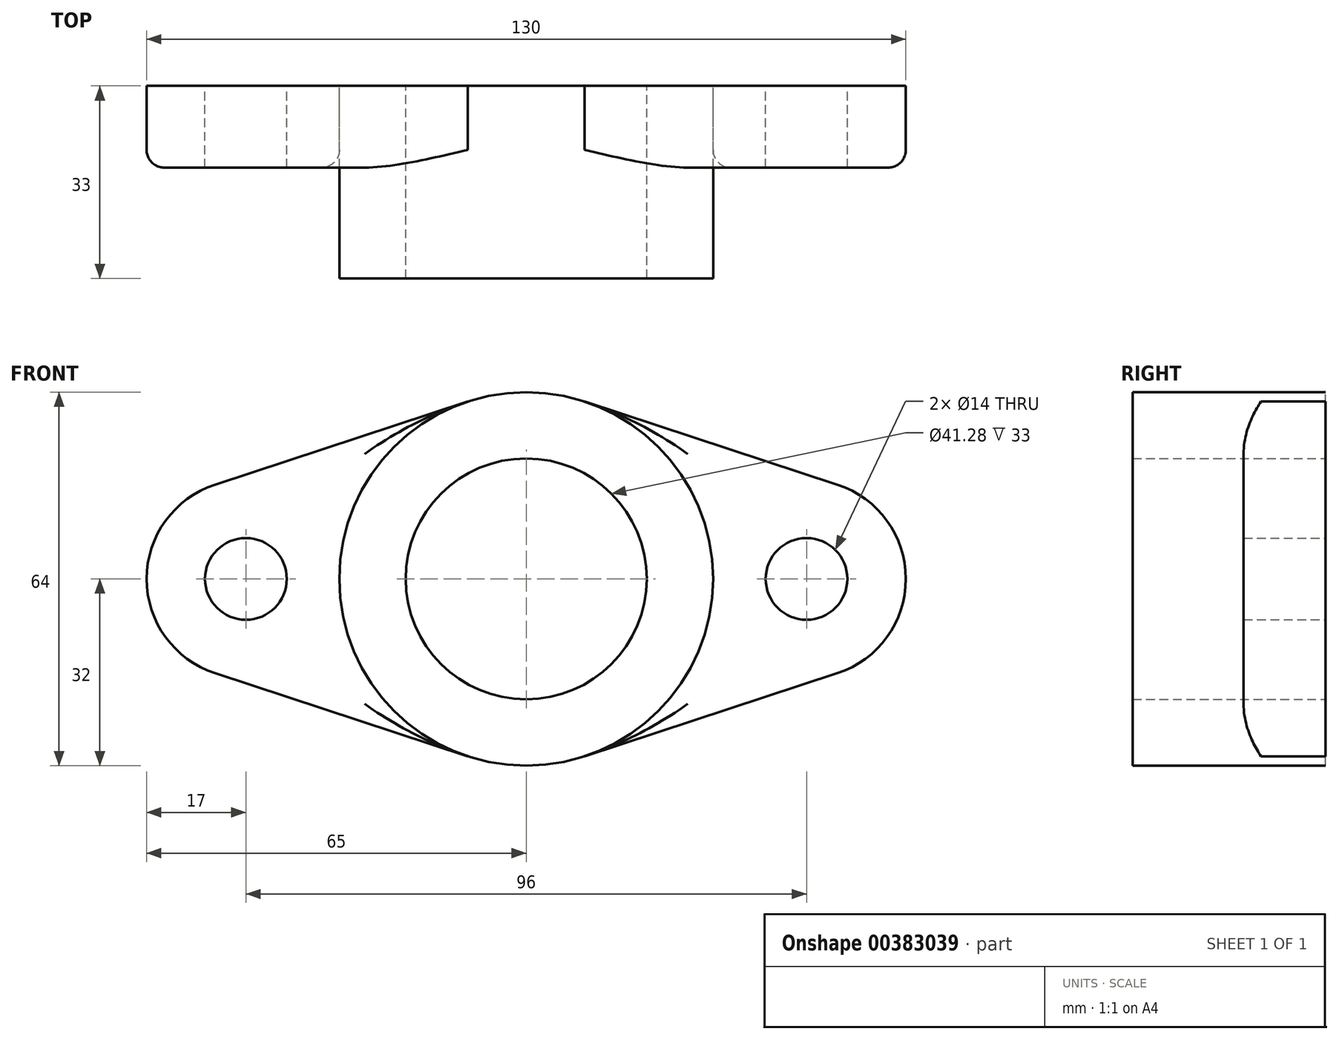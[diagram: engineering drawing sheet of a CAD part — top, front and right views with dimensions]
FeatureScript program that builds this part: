
annotation { "Feature Type Name" : "Feature", "Feature Type Description" : "" }
export const myFeature = defineFeature(function(context is Context, id is Id, definition is map)
    precondition{}
    {
        {
            var Q0;
            Q0=qCreatedBy(makeId("Front.planeOp"),FACE);
            var sketch = newSketch(context, id + "F0", { "sketchPlane" : qUnion([Q0])});
            skCircle(sketch, "E0", {"center": v(0, 0) * mm, "radius": 20.64 * mm});
            skCircle(sketch, "E1", {"center": v(-48, 0) * mm, "radius": 7 * mm});
            skCircle(sketch, "E2", {"center": v(48, 0) * mm, "radius": 7 * mm});
            skCircle(sketch, "E3", {"center": v(0, 0) * mm, "radius": 32 * mm});
            skArc(sketch, "E4", {"start": v(-53.31, 16.15) * mm, "mid": v(-65, 0) * mm, "end": v(-53.31, -16.15) * mm});
            skArc(sketch, "E5", {"start": v(53.31, -16.15) * mm, "mid": v(65, 0) * mm, "end": v(53.31, 16.15) * mm});
            skLineSegment(sketch, "E6", {"start": v(-53.31, 16.15) * mm, "end": v(-10, 30.4) * mm});
            skLineSegment(sketch, "E7", {"start": v(-53.31, -16.15) * mm, "end": v(-10, -30.4) * mm});
            skLineSegment(sketch, "E8", {"start": v(53.31, 16.15) * mm, "end": v(10, 30.4) * mm});
            skLineSegment(sketch, "E9", {"start": v(53.31, -16.15) * mm, "end": v(10, -30.4) * mm});
            skSolve(sketch);
        }
        {
            var Q0;
            Q0=makeQuery(id+"F0.imprint","IMPRINT",FACE,{"disambiguationData":[TD([[makeQuery(id+"F0.imprint","IMPRINT",EDGE,{"derivedFrom":sQuery(id+"F0.wireOp",EDGE,"E1")}),-1.0]])]});
            var Q1;
            Q1=makeQuery(id+"F0.imprint","IMPRINT",FACE,{"disambiguationData":[TD([[makeQuery(id+"F0.imprint","IMPRINT",EDGE,{"derivedFrom":sQuery(id+"F0.wireOp",EDGE,"E2")}),-1.0]])]});
            extrude(context, id + "F1", {"entities" : qUnion([Q0, Q1]), "depth" : 14 * mm});
        }
        {
            var Q0;
            Q0=makeQuery(id+"F0.imprint","IMPRINT",FACE,{"disambiguationData":[TD([[makeQuery(id+"F0.imprint","IMPRINT",EDGE,{"derivedFrom":sQuery(id+"F0.wireOp",EDGE,"E0")}),-1.0]])]});
            extrude(context, id + "F2", {"entities" : qUnion([Q0]), "depth" : 33 * mm});
        }
        {
            var Q0;
            {var subQ0=sQuery(id+"F0.wireOp",EDGE,"E3");Q0=makeQuery(id+"F1.opExtrude","CAP_EDGE",EDGE,{"disambiguationData":[OSD([subQ0]),TDD([makeQuery(id+"F0.imprint","IMPRINT",EDGE,{"disambiguationData":[TD([[makeQuery(id+"F0.imprint","INTERSECT",VERTEX,{"derivedFrom":[subQ0,sQuery(id+"F0.wireOp",EDGE,"E8")]}),1.0]])],"derivedFrom":subQ0})])],"isStart":false});}
            var Q1;
            Q1=makeQuery(id+"F1.opExtrude","CAP_EDGE",EDGE,{"disambiguationData":[OSD([sQuery(id+"F0.wireOp",EDGE,"E8")])],"isStart":false});
            var Q2;
            Q2=makeQuery(id+"F1.opExtrude","CAP_EDGE",EDGE,{"disambiguationData":[OSD([sQuery(id+"F0.wireOp",EDGE,"E5")])],"isStart":false});
            var Q3;
            Q3=makeQuery(id+"F1.opExtrude","CAP_EDGE",EDGE,{"disambiguationData":[OSD([sQuery(id+"F0.wireOp",EDGE,"E9")])],"isStart":false});
            var Q4;
            {var subQ0=sQuery(id+"F0.wireOp",EDGE,"E3");Q4=makeQuery(id+"F1.opExtrude","CAP_EDGE",EDGE,{"disambiguationData":[OSD([subQ0]),TDD([makeQuery(id+"F0.imprint","IMPRINT",EDGE,{"disambiguationData":[TD([[makeQuery(id+"F0.imprint","INTERSECT",VERTEX,{"derivedFrom":[subQ0,sQuery(id+"F0.wireOp",EDGE,"E6")]}),-1.0]])],"derivedFrom":subQ0})])],"isStart":false});}
            var Q5;
            Q5=makeQuery(id+"F1.opExtrude","CAP_EDGE",EDGE,{"disambiguationData":[OSD([sQuery(id+"F0.wireOp",EDGE,"E6")])],"isStart":false});
            var Q6;
            Q6=makeQuery(id+"F1.opExtrude","CAP_EDGE",EDGE,{"disambiguationData":[OSD([sQuery(id+"F0.wireOp",EDGE,"E4")])],"isStart":false});
            fillet(context, id + "F3", {"entities" : qUnion([Q0, Q1, Q2, Q3, Q4, Q5, Q6]), "radius" : 3 * mm, "tangentPropagation" : true, "allowEdgeOverflow" : false});
        }
    });
